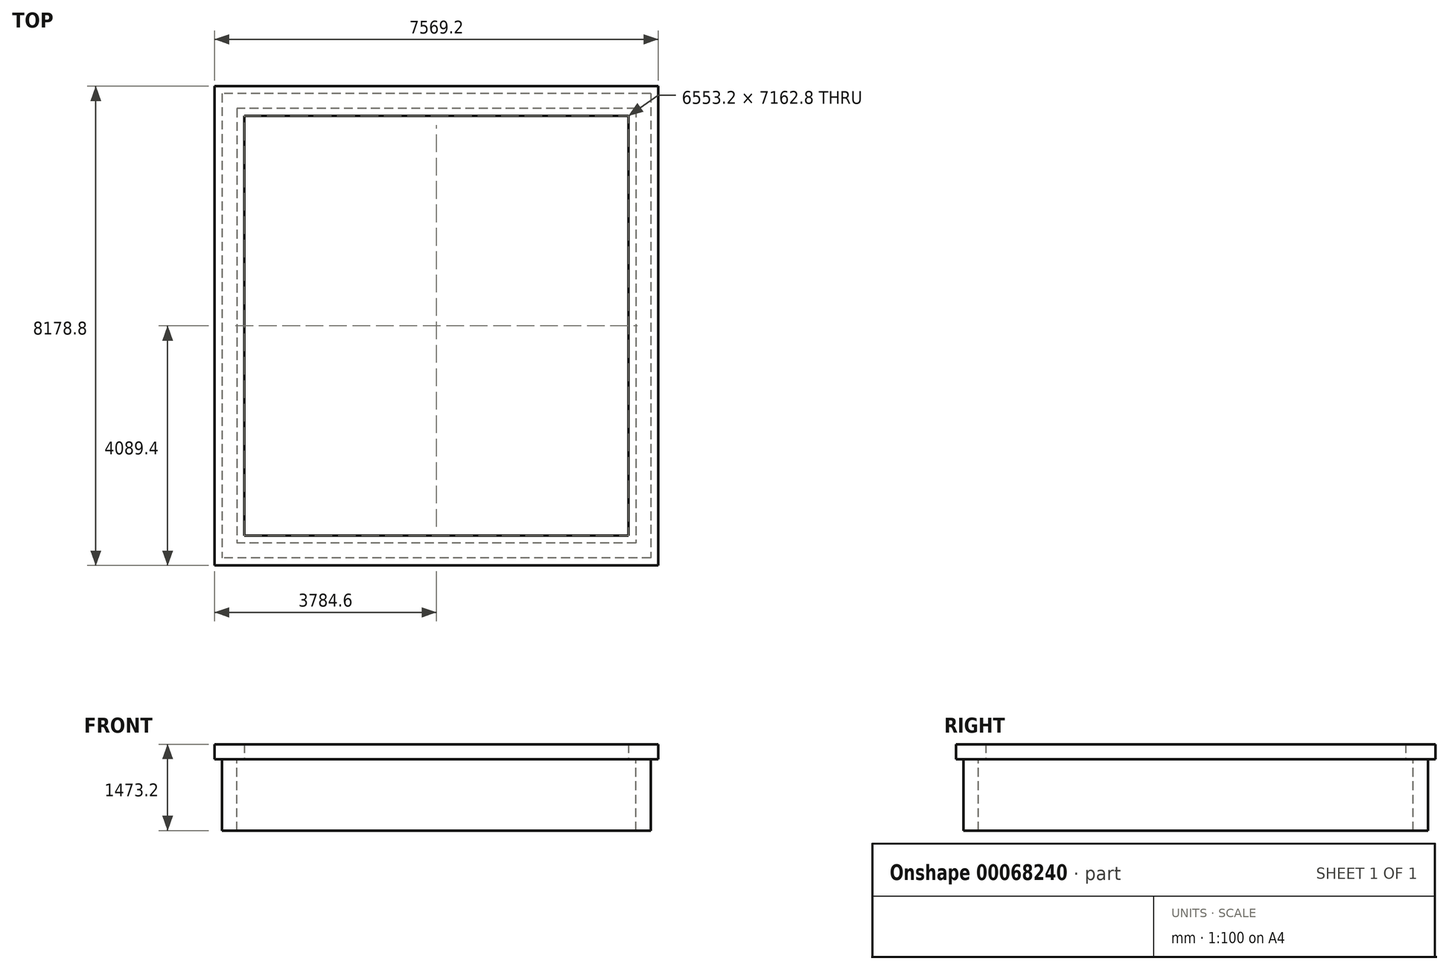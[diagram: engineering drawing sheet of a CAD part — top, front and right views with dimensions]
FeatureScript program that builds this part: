
annotation { "Feature Type Name" : "Feature", "Feature Type Description" : "" }
export const myFeature = defineFeature(function(context is Context, id is Id, definition is map)
    precondition{}
    {
        {
            var Q0;
            Q0=qCreatedBy(makeId("Top.planeOp"),FACE);
            var sketch = newSketch(context, id + "F0", { "sketchPlane" : qUnion([Q0])});
            skLineSegment(sketch, "E0.rect.bottom", {"start": v(3657.6, 3962.4) * mm, "end": v(-3657.6, 3962.4) * mm});
            skLineSegment(sketch, "E0.rect.top", {"start": v(3657.6, -3962.4) * mm, "end": v(-3657.6, -3962.4) * mm});
            skLineSegment(sketch, "E0.rect.left", {"start": v(3657.6, 3962.4) * mm, "end": v(3657.6, -3962.4) * mm});
            skLineSegment(sketch, "E0.rect.right", {"start": v(-3657.6, 3962.4) * mm, "end": v(-3657.6, -3962.4) * mm});
            skPoint(sketch, "E0.rect.middle", {"position": v(0, 0) * mm});
            skSolve(sketch);
        }
        {
            var Q0;
            Q0=makeQuery(id+"F0.imprint","IMPRINT",FACE,{"disambiguationData":[TD([[makeQuery(id+"F0.imprint","IMPRINT",EDGE,{"derivedFrom":sQuery(id+"F0.wireOp",EDGE,"E0.rect.bottom")}),1.0]])]});
            var sketch = newSketch(context, id + "F1", { "sketchPlane" : qUnion([Q0])});
            skLineSegment(sketch, "E1.rect.bottom", {"start": v(3403.6, 3708.4) * mm, "end": v(-3403.6, 3708.4) * mm});
            skLineSegment(sketch, "E1.rect.top", {"start": v(3403.6, -3708.4) * mm, "end": v(-3403.6, -3708.4) * mm});
            skLineSegment(sketch, "E1.rect.left", {"start": v(3403.6, 3708.4) * mm, "end": v(3403.6, -3708.4) * mm});
            skLineSegment(sketch, "E1.rect.right", {"start": v(-3403.6, 3708.4) * mm, "end": v(-3403.6, -3708.4) * mm});
            skPoint(sketch, "E1.rect.middle", {"position": v(0, 0) * mm});
            skSolve(sketch);
        }
        {
            var Q0;
            Q0=makeQuery(id+"F1.imprint","IMPRINT",FACE,{"disambiguationData":[TD([[makeQuery(id+"F1.imprint","IMPRINT",EDGE,{"derivedFrom":sQuery(id+"F1.wireOp",EDGE,"E1.rect.bottom")}),-1.0]])]});
            extrude(context, id + "F2", {"entities" : qUnion([Q0]), "oppositeDirection" : true, "depth" : 1219.2 * mm});
        }
        {
            var Q0;
            Q0=qCreatedBy(makeId("Top.planeOp"),FACE);
            var sketch = newSketch(context, id + "F3", { "sketchPlane" : qUnion([Q0])});
            skLineSegment(sketch, "E2.rect.bottom", {"start": v(3784.6, -4089.4) * mm, "end": v(-3784.6, -4089.4) * mm});
            skLineSegment(sketch, "E2.rect.top", {"start": v(3784.6, 4089.4) * mm, "end": v(-3784.6, 4089.4) * mm});
            skLineSegment(sketch, "E2.rect.left", {"start": v(3784.6, -4089.4) * mm, "end": v(3784.6, 4089.4) * mm});
            skLineSegment(sketch, "E2.rect.right", {"start": v(-3784.6, -4089.4) * mm, "end": v(-3784.6, 4089.4) * mm});
            skPoint(sketch, "E2.rect.middle", {"position": v(0, 0) * mm});
            skLineSegment(sketch, "E3.rect.bottom", {"start": v(3276.6, 3581.4) * mm, "end": v(-3276.6, 3581.4) * mm});
            skLineSegment(sketch, "E3.rect.top", {"start": v(3276.6, -3581.4) * mm, "end": v(-3276.6, -3581.4) * mm});
            skLineSegment(sketch, "E3.rect.left", {"start": v(3276.6, 3581.4) * mm, "end": v(3276.6, -3581.4) * mm});
            skLineSegment(sketch, "E3.rect.right", {"start": v(-3276.6, 3581.4) * mm, "end": v(-3276.6, -3581.4) * mm});
            skSolve(sketch);
        }
        {
            var Q0;
            Q0 = qSketchRegion(id + "F3", true);
            extrude(context, id + "F4", {"entities" : qUnion([Q0]), "operationType" : NewBodyOperationType.ADD, "depth" : 254 * mm});
        }
    });
